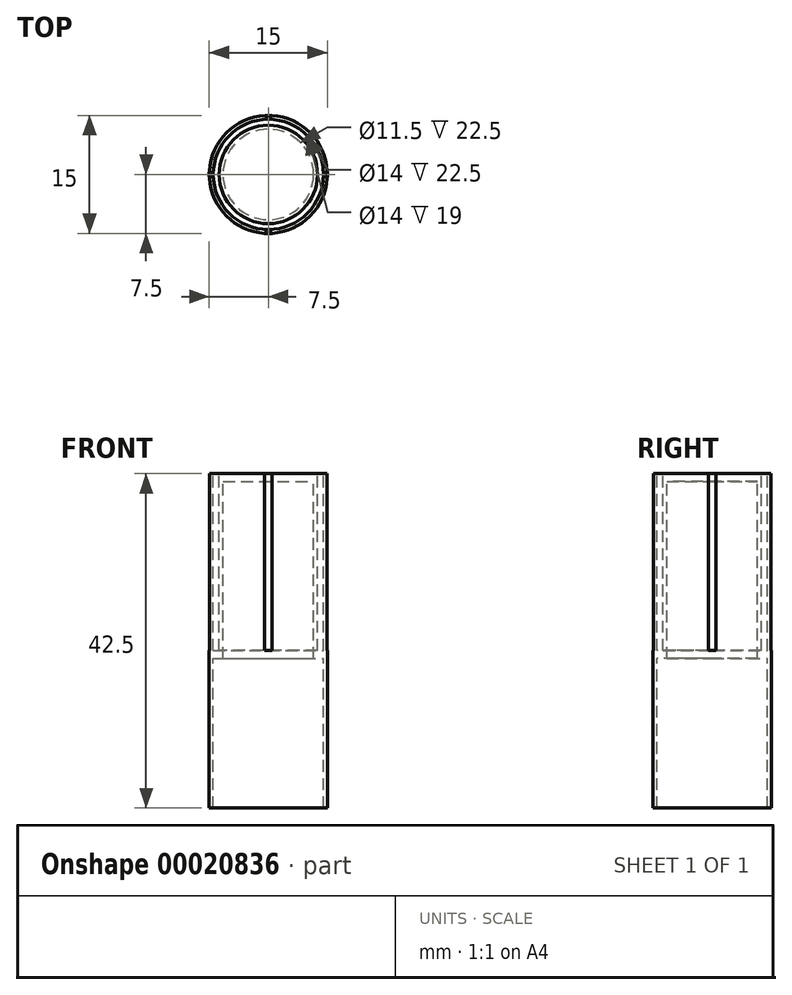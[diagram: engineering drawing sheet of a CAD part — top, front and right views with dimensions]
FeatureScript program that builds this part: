
annotation { "Feature Type Name" : "Feature", "Feature Type Description" : "" }
export const myFeature = defineFeature(function(context is Context, id is Id, definition is map)
    precondition{}
    {
        {
            var Q0;
            Q0=qCreatedBy(makeId("Top.planeOp"),FACE);
            var sketch = newSketch(context, id + "F0", { "sketchPlane" : qUnion([Q0])});
            skCircle(sketch, "E0", {"center": v(0, 0) * mm, "radius": 6.25 * mm});
            skSolve(sketch);
        }
        {
            var Q0;
            Q0 = qSketchRegion(id + "F0", true);
            extrude(context, id + "F1", {"entities" : qUnion([Q0]), "oppositeDirection" : true, "depth" : 1 * mm});
        }
        {
            var Q0;
            Q0=makeQuery(id+"F1.opExtrude","CAP_FACE",FACE,{"disambiguationData":[OSD([sQuery(id+"F0.wireOp",EDGE,"E0")])],"isStart":false});
            var sketch = newSketch(context, id + "F2", { "sketchPlane" : qUnion([Q0])});
            skCircle(sketch, "E1", {"center": v(0, 0) * mm, "radius": 6.25 * mm});
            skCircle(sketch, "E2", {"center": v(0, 0) * mm, "radius": 5.75 * mm});
            skSolve(sketch);
        }
        {
            var Q0;
            Q0 = qSketchRegion(id + "F2", true);
            extrude(context, id + "F3", {"entities" : qUnion([Q0]), "operationType" : NewBodyOperationType.ADD, "depth" : 22.5 * mm});
        }
        {
            var Q0;
            Q0=qCreatedBy(makeId("Top.planeOp"),FACE);
            var sketch = newSketch(context, id + "F4", { "sketchPlane" : qUnion([Q0])});
            skCircle(sketch, "E3", {"center": v(0, 0) * mm, "radius": 7.5 * mm});
            skCircle(sketch, "E4", {"center": v(0, 0) * mm, "radius": 7 * mm});
            skSolve(sketch);
        }
        {
            var Q0;
            Q0 = qSketchRegion(id + "F4", true);
            extrude(context, id + "F5", {"entities" : qUnion([Q0]), "oppositeDirection" : true, "depth" : 42.5 * mm});
        }
        {
            var Q0;
            Q0=makeQuery(id+"F3.opExtrude","CAP_FACE",FACE,{"disambiguationData":[OSD([sQuery(id+"F2.wireOp",EDGE,"E1"),sQuery(id+"F2.wireOp",EDGE,"E2")])],"isStart":false});
            var sketch = newSketch(context, id + "F6", { "sketchPlane" : qUnion([Q0])});
            skCircle(sketch, "E5", {"center": v(0, 0) * mm, "radius": 6.25 * mm});
            skCircle(sketch, "E6", {"center": v(0, 0) * mm, "radius": 7 * mm});
            skSolve(sketch);
        }
        {
            var Q0;
            Q0 = qSketchRegion(id + "F6", true);
            extrude(context, id + "F7", {"entities" : qUnion([Q0]), "operationType" : NewBodyOperationType.ADD, "oppositeDirection" : true, "depth" : 1 * mm});
        }
        {
            var Q0;
            Q0=qCreatedBy(makeId("Top.planeOp"),FACE);
            var sketch = newSketch(context, id + "F8", { "sketchPlane" : qUnion([Q0])});
            skLineSegment(sketch, "E7.bottom", {"start": v(-0.43, 7.52) * mm, "end": v(0.47, 7.52) * mm});
            skLineSegment(sketch, "E7.top", {"start": v(-0.43, 7.42) * mm, "end": v(0.47, 7.42) * mm});
            skLineSegment(sketch, "E7.left", {"start": v(-0.43, 7.52) * mm, "end": v(-0.43, 7.42) * mm});
            skLineSegment(sketch, "E7.right", {"start": v(0.47, 7.52) * mm, "end": v(0.47, 7.42) * mm});
            skLineSegment(sketch, "E8.rect.bottom", {"start": v(-7.41, 0.45) * mm, "end": v(-7.51, 0.45) * mm});
            skLineSegment(sketch, "E8.rect.top", {"start": v(-7.41, -0.45) * mm, "end": v(-7.51, -0.45) * mm});
            skLineSegment(sketch, "E8.rect.left", {"start": v(-7.41, 0.45) * mm, "end": v(-7.41, -0.45) * mm});
            skLineSegment(sketch, "E8.rect.right", {"start": v(-7.51, 0.45) * mm, "end": v(-7.51, -0.45) * mm});
            skPoint(sketch, "E8.rect.middle", {"position": v(-7.46, 0) * mm});
            skLineSegment(sketch, "E9.rect.bottom", {"start": v(0.45, -7.4) * mm, "end": v(-0.45, -7.4) * mm});
            skLineSegment(sketch, "E9.rect.top", {"start": v(0.45, -7.5) * mm, "end": v(-0.45, -7.5) * mm});
            skLineSegment(sketch, "E9.rect.left", {"start": v(0.45, -7.4) * mm, "end": v(0.45, -7.5) * mm});
            skLineSegment(sketch, "E9.rect.right", {"start": v(-0.45, -7.4) * mm, "end": v(-0.45, -7.5) * mm});
            skPoint(sketch, "E9.rect.middle", {"position": v(0, -7.45) * mm});
            skLineSegment(sketch, "E10.rect.bottom", {"start": v(7.4, -0.45) * mm, "end": v(7.5, -0.45) * mm});
            skLineSegment(sketch, "E10.rect.top", {"start": v(7.4, 0.45) * mm, "end": v(7.5, 0.45) * mm});
            skLineSegment(sketch, "E10.rect.left", {"start": v(7.4, -0.45) * mm, "end": v(7.4, 0.45) * mm});
            skLineSegment(sketch, "E10.rect.right", {"start": v(7.5, -0.45) * mm, "end": v(7.5, 0.45) * mm});
            skPoint(sketch, "E10.rect.middle", {"position": v(7.45, 0) * mm});
            skSolve(sketch);
        }
        {
            var Q0;
            Q0 = qSketchRegion(id + "F8", true);
            extrude(context, id + "F9", {"entities" : qUnion([Q0]), "operationType" : NewBodyOperationType.REMOVE, "oppositeDirection" : true, "depth" : 22.5 * mm});
        }
        {
            var Q0;
            Q0 = qSketchRegion(id + "F8", true);
            extrude(context, id + "F10", {"entities" : qUnion([Q0]), "operationType" : NewBodyOperationType.REMOVE, "oppositeDirection" : true, "depth" : 22.5 * mm});
        }
        {
            var Q0;
            Q0 = qSketchRegion(id + "F8", true);
            extrude(context, id + "F11", {"entities" : qUnion([Q0]), "operationType" : NewBodyOperationType.REMOVE, "oppositeDirection" : true, "depth" : 22.5 * mm});
        }
        {
            var Q0;
            Q0 = qSketchRegion(id + "F8", true);
            extrude(context, id + "F12", {"entities" : qUnion([Q0]), "operationType" : NewBodyOperationType.REMOVE, "oppositeDirection" : true, "depth" : 22.5 * mm});
        }
    });
